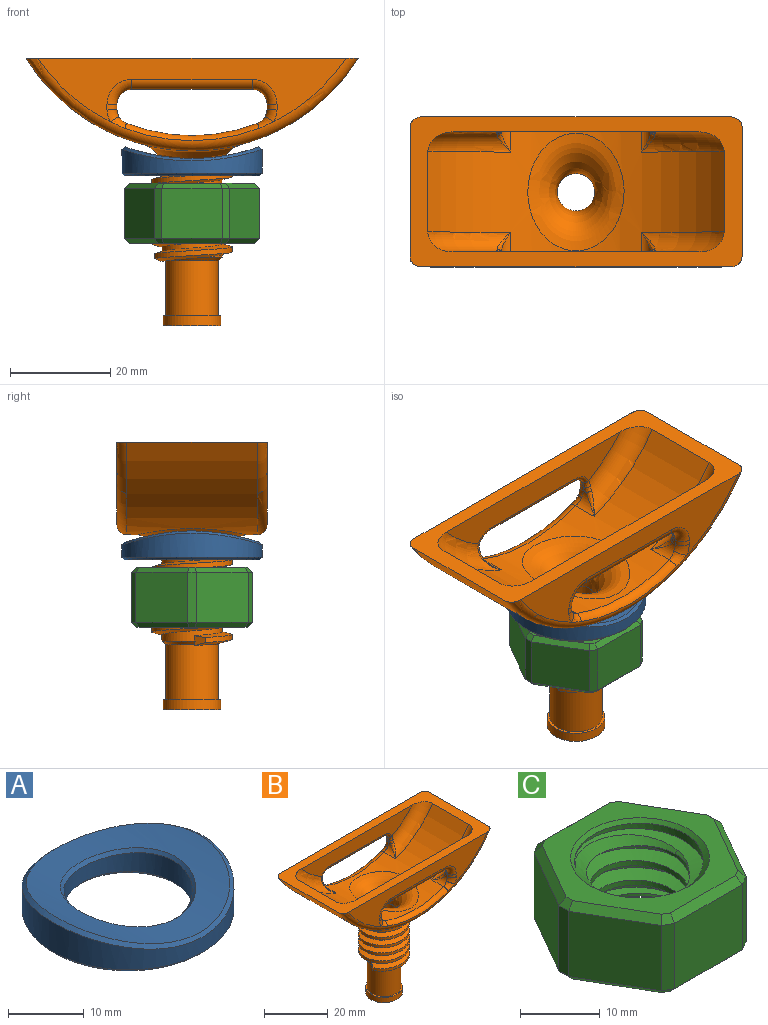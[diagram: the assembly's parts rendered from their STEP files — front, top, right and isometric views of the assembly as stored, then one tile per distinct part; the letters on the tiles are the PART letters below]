
ASSEMBLY  parts=3 mates=2
PART A: 8 faces, bbox 28x28x5.8 mm
  f0: cylinder r=40mm len=27.01mm, axis (0,1,0), area 321.3mm2, adj f6,f7
  f1: cylinder r=14mm len=28mm, axis (0,0,1), area 319.1mm2, adj f4,f7
  f2: plane 27x27mm, normal (0,0,-1), area 318.1mm2, adj f4,f5
  f3: cylinder r=8.5mm len=17mm, axis (0,0,1), area 186mm2, adj f5,f6
  f4: cone r=14mm half-angle=45deg, axis (0,0,1), area 61.1mm2, adj f1,f2
  f5: cone r=9mm half-angle=45deg, axis (0,0,-1), area 38.9mm2, adj f2,f3
  f6: bspline ~17.99x17.76mm, area 36.6mm2, adj f0,f3
  f7: bspline ~28x28mm, area 66.4mm2, adj f0,f1
PART B: 80 faces, bbox 72.4x31.1x57.9 mm
  f0: cylinder r=36mm len=59.18mm, axis (0,1,0), area 1035mm2, adj f4,f14,f27,f28,f32,f33,f35,f36
  f1: cylinder r=6mm len=17.65mm, axis (0,0,1), area 224.6mm2, adj f2,f13,f15,f16,f17,f18,f79
  f2: bspline ~22.03x19.52mm, area 322.2mm2, adj f1,f3,f7,f16,f17
  f3: cylinder r=39mm len=66.35mm, axis (0,1,0), area 1722.5mm2, adj f2,f4,f39,f40
  f4: plane 66.89x30.53mm, normal (0,0,1), area 583.1mm2, adj f0,f3,f5,f6,f23,f26,f35,f36
  f5: plane 61.6x12.68mm, normal (0,-1,0), area 355mm2, adj f4,f40,f54,f55,f56,f57,f58,f59
  f6: plane 61.6x12.68mm, normal (0,1,0), area 355mm2, adj f4,f39,f44,f45,f46,f47,f48,f49
  f7: cylinder r=6mm len=3.96mm, axis (0,0,1), area 0.2mm2, adj f2,f17
  f8: plane 11.5x11.5mm, normal (0,0,-1), area 59.7mm2, adj f9,f12
  f9: cylinder r=5.75mm len=11.5mm, axis (0,0,1), area 72.3mm2, adj f8,f10
  f10: plane 11.5x11.5mm, normal (0,0,1), area 17.3mm2, adj f9,f11
  f11: cylinder r=5.25mm len=11mm, axis (0,0,1), area 362.9mm2, adj f10,f15
  f12: cylinder r=3.75mm len=31.6mm, axis (0,0,1), area 725.6mm2, adj f8,f14
  f13: bspline ~7.13x6.14mm, area 0mm2, adj f1,f18
  f14: bspline ~23.51x19.25mm, area 450.2mm2, adj f0,f12
  f15: cone r=6.25mm half-angle=45deg, axis (0,0,1), area 37.5mm2, adj f1,f11,f19
  f16: plane 1.97x1.51mm, normal (-0.67,-0.74,0), area 2.8mm2, adj f1,f2,f17,f18,f20
  f17: bspline ~18.5x18.48mm, area 529.7mm2, adj f1,f2,f7,f16,f20,f79
  f18: bspline ~18.5x18.48mm, area 531.7mm2, adj f1,f13,f16,f19,f20,f79
  f19: cylinder r=6mm len=8.49mm, axis (0,0,1), area 5.3mm2, adj f15,f18,f79
  f20: cylinder r=8mm len=18.49mm, axis (0,0,1), area 292.4mm2, adj f16,f17,f18,f79
  f21: plane 1.02x0.76mm, normal (1,0,0), area 0.5mm2, adj f31,f32,f47,f62
  f22: plane 1.02x0.76mm, normal (-1,0,0), area 0.5mm2, adj f33,f34,f46,f68
  f23: plane 49.14x7.45mm, normal (0,-1,0), area 242.7mm2, adj f4,f37,f38,f64,f65,f66
  f24: plane 1.02x0.76mm, normal (1,0,0), area 0.5mm2, adj f27,f30,f57,f71
  f25: plane 1.02x0.76mm, normal (-1,0,0), area 0.5mm2, adj f28,f29,f56,f77
  f26: plane 49.14x7.45mm, normal (0,1,0), area 242.7mm2, adj f4,f35,f36,f73,f74,f75
  f27: cylinder r=3mm len=5.27mm, axis (0,1,0), area 10.6mm2, adj f0,f24,f53,f55,f70
  f28: cylinder r=3mm len=5.27mm, axis (0,1,0), area 10.6mm2, adj f0,f25,f52,f54,f78
  f29: cylinder r=3mm len=1.33mm, axis (0,1,0), area 0.2mm2, adj f25,f58,f76
  f30: cylinder r=3mm len=1.33mm, axis (0,1,0), area 0.2mm2, adj f24,f59,f72
  f31: cylinder r=3mm len=1.33mm, axis (0,-1,0), area 0.2mm2, adj f21,f49,f63
  f32: cylinder r=3mm len=5.27mm, axis (0,1,0), area 10.6mm2, adj f0,f21,f43,f45,f61
  f33: cylinder r=3mm len=5.27mm, axis (0,1,0), area 10.6mm2, adj f0,f22,f42,f44,f69
  f34: cylinder r=3mm len=1.33mm, axis (0,-1,0), area 0.2mm2, adj f22,f48,f67
  f35: torus R=32mm, axis (0,-1,0), area 105.4mm2, adj f0,f4,f26,f70,f71,f72
  f36: torus R=32mm, axis (0,-1,0), area 105.4mm2, adj f0,f4,f26,f76,f77,f78
  f37: torus R=32mm, axis (0,1,0), area 105.4mm2, adj f0,f4,f23,f67,f68,f69
  f38: torus R=32mm, axis (0,1,0), area 105.4mm2, adj f0,f4,f23,f61,f62,f63
  f39: torus R=37mm, axis (0,-1,0), area 240.6mm2, adj f3,f4,f6,f41,f42,f43
  f40: torus R=37mm, axis (0,-1,0), area 240.6mm2, adj f3,f4,f5,f51,f52,f53
  f41: torus R=38mm, axis (0,1,0), area 56.7mm2, adj f0,f39,f42,f43
  f42: bspline ~3.59x2.48mm, area 5.8mm2, adj f33,f39,f41,f44
  f43: bspline ~3.59x2.48mm, area 5.8mm2, adj f32,f39,f41,f45
  f44: torus R=5mm, axis (0,-1,0), area 6mm2, adj f6,f33,f42,f46
  f45: torus R=5mm, axis (0,-1,0), area 6mm2, adj f6,f32,f43,f47
  f46: cylinder r=2mm len=2mm, axis (0,0,-1), area 3.2mm2, adj f6,f22,f44,f48
  f47: cylinder r=2mm len=2mm, axis (0,0,1), area 3.2mm2, adj f6,f21,f45,f49
  f48: torus R=5mm, axis (0,-1,0), area 18.4mm2, adj f6,f34,f46,f50,f66
  f49: torus R=5mm, axis (0,-1,0), area 18.4mm2, adj f6,f31,f47,f50,f64
  f50: cylinder r=2mm len=24mm, axis (1,0,0), area 75.4mm2, adj f6,f48,f49,f65
  f51: torus R=38mm, axis (0,-1,0), area 56.7mm2, adj f0,f40,f52,f53
  f52: bspline ~3.59x2.48mm, area 5.8mm2, adj f28,f40,f51,f54
  f53: bspline ~3.59x2.48mm, area 5.8mm2, adj f27,f40,f51,f55
  f54: torus R=5mm, axis (0,-1,0), area 6mm2, adj f5,f28,f52,f56
  f55: torus R=5mm, axis (0,-1,0), area 6mm2, adj f5,f27,f53,f57
  f56: cylinder r=2mm len=2mm, axis (0,0,1), area 3.2mm2, adj f5,f25,f54,f58
  f57: cylinder r=2mm len=2mm, axis (0,0,-1), area 3.2mm2, adj f5,f24,f55,f59
  f58: torus R=5mm, axis (0,-1,0), area 18.4mm2, adj f5,f29,f56,f60,f75
  f59: torus R=5mm, axis (0,-1,0), area 18.4mm2, adj f5,f30,f57,f60,f73
  f60: cylinder r=2mm len=24mm, axis (-1,0,0), area 75.4mm2, adj f5,f58,f59,f74
  f61: bspline ~4.59x3.87mm, area 2.4mm2, adj f32,f38,f62
  f62: bspline ~2.99x2.04mm, area 1.4mm2, adj f21,f38,f61,f63
  f63: bspline ~2.47x1.46mm, area 2.1mm2, adj f31,f38,f62,f64
  f64: torus R=4mm, axis (0,1,0), area 5.9mm2, adj f23,f49,f63,f65
  f65: cylinder r=1mm len=24mm, axis (1,0,0), area 37.7mm2, adj f23,f50,f64,f66
  f66: torus R=4mm, axis (0,1,0), area 5.9mm2, adj f23,f48,f65,f67
  f67: bspline ~2.47x1.46mm, area 2.1mm2, adj f34,f37,f66,f68
  f68: bspline ~2.99x2.04mm, area 1.4mm2, adj f22,f37,f67,f69
  f69: bspline ~4.59x3.87mm, area 2.4mm2, adj f33,f37,f68
  f70: bspline ~4.59x3.87mm, area 2.4mm2, adj f27,f35,f71
  f71: bspline ~2.99x2.04mm, area 1.4mm2, adj f24,f35,f70,f72
  f72: bspline ~2.47x1.46mm, area 2.1mm2, adj f30,f35,f71,f73
  f73: torus R=4mm, axis (0,-1,0), area 5.9mm2, adj f26,f59,f72,f74
  f74: cylinder r=1mm len=24mm, axis (1,0,0), area 37.7mm2, adj f26,f60,f73,f75
  f75: torus R=4mm, axis (0,-1,0), area 5.9mm2, adj f26,f58,f74,f76
  f76: bspline ~2.47x1.46mm, area 2.1mm2, adj f29,f36,f75,f77
  f77: bspline ~2.99x2.04mm, area 1.4mm2, adj f25,f36,f76,f78
  f78: bspline ~4.59x3.87mm, area 2.4mm2, adj f28,f36,f77
  f79: plane 2.52x2.31mm, normal (-0.82,0.58,0), area 4.1mm2, adj f1,f17,f18,f19,f20
PART C: 46 faces, bbox 27x24.2x12.2 mm
  f0: plane 25x22.25mm, normal (0,0,1), area 189.7mm2, adj f5,f22,f23,f24,f25,f26,f27,f28
  f1: cylinder r=6.2mm len=12.4mm, axis (0,0,-1), area 72.8mm2, adj f3,f5,f6,f7,f9
  f2: plane 25x22.25mm, normal (0,0,-1), area 189.7mm2, adj f4,f34,f35,f36,f37,f38,f39,f40
  f3: cone r=6.2mm half-angle=45deg, axis (0,0,-1), area 12.8mm2, adj f1,f4,f7,f9
  f4: cone r=6.2mm half-angle=45deg, axis (0,0,-1), area 81.2mm2, adj f2,f3,f7,f8,f9
  f5: cone r=8.7mm half-angle=45deg, axis (0,0,1), area 92.8mm2, adj f0,f1,f6,f7,f8,f9
  f6: cone r=8.7mm half-angle=45deg, axis (0,0,1), area 1.1mm2, adj f1,f5,f9
  f7: bspline ~18.94x16.4mm, area 283.6mm2, adj f1,f3,f4,f5,f8
  f8: cylinder r=8.2mm len=16.4mm, axis (0,0,1), area 229.8mm2, adj f4,f5,f7,f9
  f9: bspline ~18.94x16.4mm, area 283.2mm2, adj f1,f3,f4,f5,f6,f8
  f10: plane 12x10mm, normal (0,1,0), area 120mm2, adj f16,f17,f24,f35
  f11: plane 10.39x10mm, normal (0.87,0.5,0), area 120mm2, adj f17,f18,f28,f39
  f12: plane 10.39x10mm, normal (0.87,-0.5,0), area 120mm2, adj f18,f20,f32,f43
  f13: plane 12x10mm, normal (0,-1,0), area 120mm2, adj f20,f21,f31,f44
  f14: plane 10.39x10mm, normal (-0.87,-0.5,0), area 120mm2, adj f19,f21,f27,f40
  f15: plane 10.39x10mm, normal (-0.87,0.5,0), area 120mm2, adj f16,f19,f23,f36
  f16: plane 10x1.5mm, normal (-0.5,0.87,0), area 17.3mm2, adj f10,f15,f22,f34
  f17: plane 10x1.5mm, normal (0.5,0.87,0), area 17.3mm2, adj f10,f11,f26,f37
  f18: plane 10x1.73mm, normal (1,0,0), area 17.3mm2, adj f11,f12,f30,f41
  f19: plane 10x1.73mm, normal (-1,0,0), area 17.3mm2, adj f14,f15,f25,f38
  f20: plane 10x1.5mm, normal (0.5,-0.87,0), area 17.3mm2, adj f12,f13,f33,f45
  f21: plane 10x1.5mm, normal (-0.5,-0.87,0), area 17.3mm2, adj f13,f14,f29,f42
  f22: plane 1.77x1.6mm, normal (-0.35,0.61,0.71), area 2.1mm2, adj f0,f16,f23,f24
  f23: plane 10.66x6.73mm, normal (-0.61,0.35,0.71), area 16.6mm2, adj f0,f15,f22,f25
  f24: plane 12x1mm, normal (0,0.71,0.71), area 16.6mm2, adj f0,f10,f22,f26
  f25: plane 1.73x1mm, normal (-0.71,0,0.71), area 2.1mm2, adj f0,f19,f23,f27
  f26: plane 1.77x1.6mm, normal (0.35,0.61,0.71), area 2.1mm2, adj f0,f17,f24,f28
  f27: plane 10.66x6.73mm, normal (-0.61,-0.35,0.71), area 16.6mm2, adj f0,f14,f25,f29
  f28: plane 10.66x6.73mm, normal (0.61,0.35,0.71), area 16.6mm2, adj f0,f11,f26,f30
  f29: plane 1.77x1.6mm, normal (-0.35,-0.61,0.71), area 2.1mm2, adj f0,f21,f27,f31
  f30: plane 1.73x1mm, normal (0.71,0,0.71), area 2.1mm2, adj f0,f18,f28,f32
  f31: plane 12x1mm, normal (0,-0.71,0.71), area 16.6mm2, adj f0,f13,f29,f33
  f32: plane 10.66x6.73mm, normal (0.61,-0.35,0.71), area 16.6mm2, adj f0,f12,f30,f33
  f33: plane 1.77x1.6mm, normal (0.35,-0.61,0.71), area 2.1mm2, adj f0,f20,f31,f32
  f34: plane 1.77x1.6mm, normal (-0.35,0.61,-0.71), area 2.1mm2, adj f2,f16,f35,f36
  f35: plane 12x1mm, normal (0,0.71,-0.71), area 16.6mm2, adj f2,f10,f34,f37
  f36: plane 10.66x6.73mm, normal (-0.61,0.35,-0.71), area 16.6mm2, adj f2,f15,f34,f38
  f37: plane 1.77x1.6mm, normal (0.35,0.61,-0.71), area 2.1mm2, adj f2,f17,f35,f39
  f38: plane 1.73x1mm, normal (-0.71,0,-0.71), area 2.1mm2, adj f2,f19,f36,f40
  f39: plane 10.66x6.73mm, normal (0.61,0.35,-0.71), area 16.6mm2, adj f2,f11,f37,f41
  f40: plane 10.66x6.73mm, normal (-0.61,-0.35,-0.71), area 16.6mm2, adj f2,f14,f38,f42
  f41: plane 1.73x1mm, normal (0.71,0,-0.71), area 2.1mm2, adj f2,f18,f39,f43
  f42: plane 1.77x1.6mm, normal (-0.35,-0.61,-0.71), area 2.1mm2, adj f2,f21,f40,f44
  f43: plane 10.66x6.73mm, normal (0.61,-0.35,-0.71), area 16.6mm2, adj f2,f12,f41,f45
  f44: plane 12x1mm, normal (0,-0.71,-0.71), area 16.6mm2, adj f2,f13,f42,f45
  f45: plane 1.77x1.6mm, normal (0.35,-0.61,-0.71), area 2.1mm2, adj f2,f20,f43,f44
PLACE A t=(0,0,-5)mm
PLACE B at identity fixed
PLACE C t=(0,0,-18.5)mm
MATE fastened A.f1 <-> B.f12  axis (0,0,-1) through (0,0,-5)mm
MATE fastened C.f1 <-> B.f12  axis (0,0,-1) through (0,0,-18.5)mm
